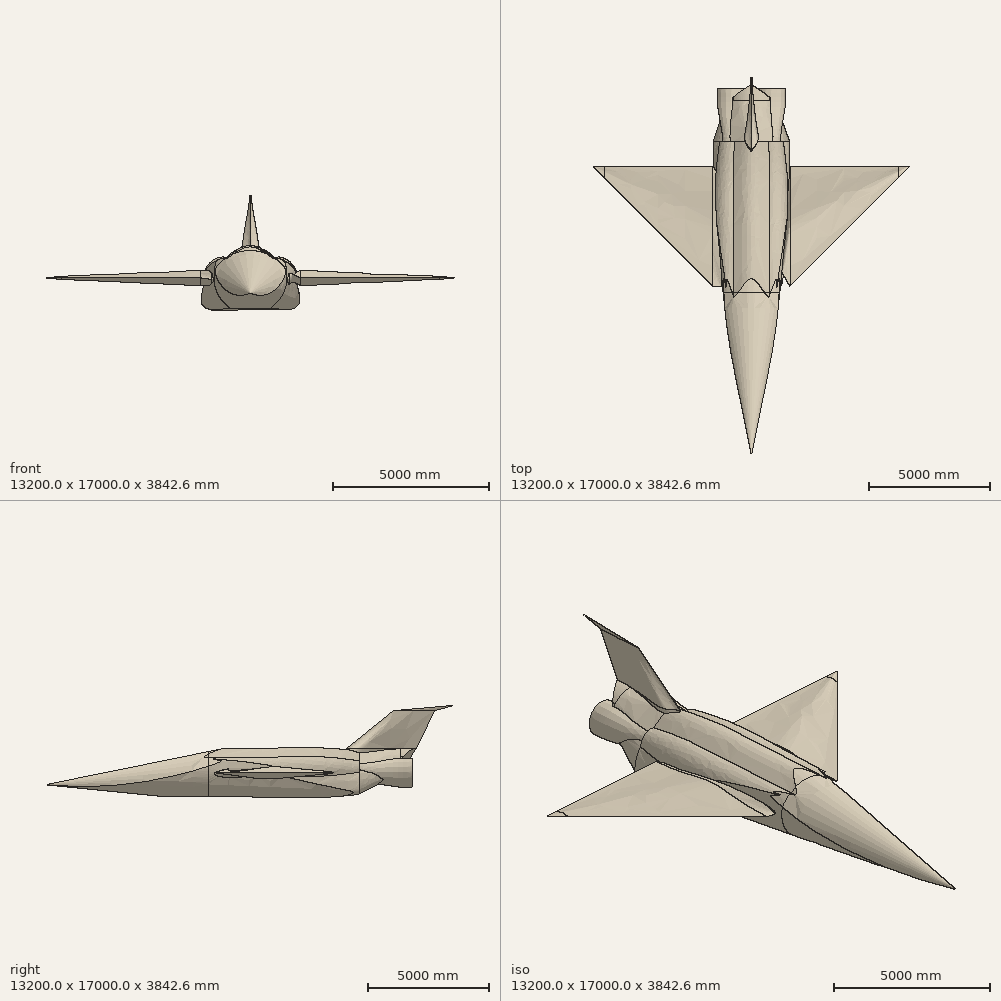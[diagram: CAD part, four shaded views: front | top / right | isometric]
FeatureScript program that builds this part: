
annotation { "Feature Type Name" : "Feature", "Feature Type Description" : "" }
export const myFeature = defineFeature(function(context is Context, id is Id, definition is map)
    precondition{}
    {
        {
            var Q0;
            Q0=qCreatedBy(makeId("Front.planeOp"),FACE);
            cPlane(context, id + "F0", {"entities" : qUnion([Q0]), "cplaneType" : CPlaneType.OFFSET, "offset" : 1750 * mm, "width" : 152.4 * mm, "height" : 152.4 * mm});
        }
        {
            var Q0;
            Q0=qCreatedBy(id+"F0.planeOp",FACE);
            var sketch = newSketch(context, id + "F1", { "sketchPlane" : qUnion([Q0])});
            skLineSegment(sketch, "E0.top", {"start": v(-1394.2, -1000) * mm, "end": v(1394.2, -1000) * mm});
            skPoint(sketch, "E0.middle", {"position": v(0, 0) * mm});
            skFitSpline(sketch, "E1", {"points": [v(-1600, -1000) * mm, v(-848, 530) * mm, v(0, 1000) * mm, v(848, 530) * mm, v(1600, -1000) * mm], "startDerivative": vector(0, 10524.75) * mm, "endDerivative": vector(0, -10524.75) * mm});
            skArc(sketch, "E2", {"start": v(-735.27, 618.52) * mm, "mid": v(-1273.27, 435.52) * mm, "end": v(-1440.68, -107.53) * mm});
            skArc(sketch, "E3.trimOffspring", {"start": v(1440.68, -107.53) * mm, "mid": v(1273.27, 435.52) * mm, "end": v(735.27, 618.52) * mm});
            skFitSpline(sketch, "E4.trimOffspring", {"points": [v(-1600, -1000) * mm, v(-848, 530) * mm, v(0, 1000) * mm, v(848, 530) * mm, v(1600, -1000) * mm], "startDerivative": vector(0, 10524.75) * mm, "endDerivative": vector(0, -10524.75) * mm});
            skFitSpline(sketch, "E5.trimOffspring", {"points": [v(-1600, -1000) * mm, v(-848, 530) * mm, v(0, 1000) * mm, v(848, 530) * mm, v(1600, -1000) * mm], "startDerivative": vector(0, 10524.75) * mm, "endDerivative": vector(0, -10524.75) * mm});
            skArc(sketch, "E6.filletArc", {"start": v(-1593.82, -787.83) * mm, "mid": v(-1539.85, -937.05) * mm, "end": v(-1394.2, -1000) * mm});
            skArc(sketch, "E7.filletArc", {"start": v(1394.2, -1000) * mm, "mid": v(1539.85, -937.05) * mm, "end": v(1593.82, -787.83) * mm});
            skSolve(sketch);
        }
        {
            var Q0;
            Q0=qCreatedBy(makeId("Front.planeOp"),FACE);
            var sketch = newSketch(context, id + "F2", { "sketchPlane" : qUnion([Q0])});
            skLineSegment(sketch, "E8.top", {"start": v(-1394.2, -1000) * mm, "end": v(1394.2, -1000) * mm});
            skPoint(sketch, "E8.middle", {"position": v(0, 0) * mm});
            skFitSpline(sketch, "E9", {"points": [v(-1600, -1000) * mm, v(-848, 530) * mm, v(0, 1000) * mm, v(848, 530) * mm, v(1600, -1000) * mm], "startDerivative": vector(0, 10524.75) * mm, "endDerivative": vector(0, -10524.75) * mm});
            skArc(sketch, "E10", {"start": v(-735.27, 618.52) * mm, "mid": v(-1273.27, 435.52) * mm, "end": v(-1440.68, -107.53) * mm});
            skArc(sketch, "E11.trimOffspring", {"start": v(1440.68, -107.53) * mm, "mid": v(1273.27, 435.52) * mm, "end": v(735.27, 618.52) * mm});
            skFitSpline(sketch, "E12.trimOffspring", {"points": [v(-1600, -1000) * mm, v(-848, 530) * mm, v(0, 1000) * mm, v(848, 530) * mm, v(1600, -1000) * mm], "startDerivative": vector(0, 10524.75) * mm, "endDerivative": vector(0, -10524.75) * mm});
            skFitSpline(sketch, "E13.trimOffspring", {"points": [v(-1600, -1000) * mm, v(-848, 530) * mm, v(0, 1000) * mm, v(848, 530) * mm, v(1600, -1000) * mm], "startDerivative": vector(0, 10524.75) * mm, "endDerivative": vector(0, -10524.75) * mm});
            skArc(sketch, "E14.filletArc", {"start": v(-1593.82, -787.83) * mm, "mid": v(-1539.85, -937.05) * mm, "end": v(-1394.2, -1000) * mm});
            skArc(sketch, "E15.filletArc", {"start": v(1394.2, -1000) * mm, "mid": v(1539.85, -937.05) * mm, "end": v(1593.82, -787.83) * mm});
            skSolve(sketch);
        }
        {
            var Q0;
            Q0=qCreatedBy(makeId("Front.planeOp"),FACE);
            cPlane(context, id + "F3", {"entities" : qUnion([Q0]), "cplaneType" : CPlaneType.OFFSET, "offset" : 3500 * mm, "oppositeDirection" : true, "width" : 150 * mm, "height" : 150 * mm});
        }
        {
            var Q0;
            Q0=qCreatedBy(id+"F3.planeOp",FACE);
            var sketch = newSketch(context, id + "F4", { "sketchPlane" : qUnion([Q0])});
            skLineSegment(sketch, "E16.top", {"start": v(-1394.2, -1000) * mm, "end": v(1394.2, -1000) * mm});
            skPoint(sketch, "E16.middle", {"position": v(0, 0) * mm});
            skFitSpline(sketch, "E17", {"points": [v(-1600, -1000) * mm, v(-848, 530) * mm, v(0, 1000) * mm, v(848, 530) * mm, v(1600, -1000) * mm], "startDerivative": vector(0, 10524.75) * mm, "endDerivative": vector(0, -10524.75) * mm});
            skArc(sketch, "E18", {"start": v(-735.27, 618.52) * mm, "mid": v(-1273.27, 435.52) * mm, "end": v(-1440.68, -107.53) * mm});
            skArc(sketch, "E19.trimOffspring", {"start": v(1440.68, -107.53) * mm, "mid": v(1273.27, 435.52) * mm, "end": v(735.27, 618.52) * mm});
            skFitSpline(sketch, "E20.trimOffspring", {"points": [v(-1600, -1000) * mm, v(-848, 530) * mm, v(0, 1000) * mm, v(848, 530) * mm, v(1600, -1000) * mm], "startDerivative": vector(0, 10524.75) * mm, "endDerivative": vector(0, -10524.75) * mm});
            skFitSpline(sketch, "E21.trimOffspring", {"points": [v(-1600, -1000) * mm, v(-848, 530) * mm, v(0, 1000) * mm, v(848, 530) * mm, v(1600, -1000) * mm], "startDerivative": vector(0, 10524.75) * mm, "endDerivative": vector(0, -10524.75) * mm});
            skArc(sketch, "E22.filletArc", {"start": v(-1593.82, -787.83) * mm, "mid": v(-1539.85, -937.05) * mm, "end": v(-1394.2, -1000) * mm});
            skArc(sketch, "E23.filletArc", {"start": v(1394.2, -1000) * mm, "mid": v(1539.85, -937.05) * mm, "end": v(1593.82, -787.83) * mm});
            skSolve(sketch);
        }
        {
            var Q0;
            Q0=qCreatedBy(makeId("Front.planeOp"),FACE);
            cPlane(context, id + "F5", {"entities" : qUnion([Q0]), "cplaneType" : CPlaneType.OFFSET, "offset" : 4500 * mm, "oppositeDirection" : true, "width" : 150 * mm, "height" : 150 * mm});
        }
        {
            var Q0;
            Q0=qCreatedBy(id+"F5.planeOp",FACE);
            var sketch = newSketch(context, id + "F6", { "sketchPlane" : qUnion([Q0])});
            skLineSegment(sketch, "E24.top", {"start": v(-1413.07, -900) * mm, "end": v(1413.07, -900) * mm});
            skPoint(sketch, "E24.middle", {"position": v(0, 0) * mm});
            skFitSpline(sketch, "E25", {"points": [v(-1600, -900) * mm, v(-784.42, 441.24) * mm, v(0, 900) * mm, v(784.42, 441.24) * mm, v(1600, -900) * mm], "startDerivative": vector(0, 9508.62) * mm, "endDerivative": vector(0, -9508.62) * mm});
            skArc(sketch, "E26", {"start": v(-719.25, 488.69) * mm, "mid": v(-1131.76, 394.84) * mm, "end": v(-1324.66, 18.33) * mm});
            skArc(sketch, "E27.trimOffspring", {"start": v(1324.66, 18.33) * mm, "mid": v(1131.76, 394.84) * mm, "end": v(719.25, 488.69) * mm});
            skFitSpline(sketch, "E28.trimOffspring", {"points": [v(-1600, -900) * mm, v(-784.42, 441.24) * mm, v(0, 900) * mm, v(784.42, 441.24) * mm, v(1600, -900) * mm], "startDerivative": vector(0, 9508.62) * mm, "endDerivative": vector(0, -9508.62) * mm});
            skFitSpline(sketch, "E29.trimOffspring", {"points": [v(-1600, -900) * mm, v(-784.42, 441.24) * mm, v(0, 900) * mm, v(784.42, 441.24) * mm, v(1600, -900) * mm], "startDerivative": vector(0, 9508.62) * mm, "endDerivative": vector(0, -9508.62) * mm});
            skArc(sketch, "E30.filletArc", {"start": v(-1592.48, -705.43) * mm, "mid": v(-1545.4, -842.02) * mm, "end": v(-1413.07, -900) * mm});
            skArc(sketch, "E31.filletArc", {"start": v(1413.07, -900) * mm, "mid": v(1545.4, -842.02) * mm, "end": v(1592.48, -705.43) * mm});
            skLineSegment(sketch, "E32", {"start": v(-719.25, 488.69) * mm, "end": v(-1324.66, 18.33) * mm, "construction": true});
            skLineSegment(sketch, "E33", {"start": v(719.25, 488.69) * mm, "end": v(1324.66, 18.33) * mm, "construction": true});
            skSolve(sketch);
        }
        {
            var Q0;
            Q0=qCreatedBy(makeId("Front.planeOp"),FACE);
            cPlane(context, id + "F7", {"entities" : qUnion([Q0]), "cplaneType" : CPlaneType.OFFSET, "offset" : 6232.05 * mm, "oppositeDirection" : true, "width" : 150 * mm, "height" : 150 * mm});
        }
        {
            var Q0;
            Q0=qCreatedBy(id+"F7.planeOp",FACE);
            var sketch = newSketch(context, id + "F8", { "sketchPlane" : qUnion([Q0])});
            skArc(sketch, "E34", {"start": v(998.61, 52.63) * mm, "mid": v(0, 1000) * mm, "end": v(-998.61, 52.63) * mm});
            skLineSegment(sketch, "E35", {"start": v(0, 0) * mm, "end": v(-948.68, 0) * mm});
            skLineSegment(sketch, "E36", {"start": v(0, 0) * mm, "end": v(948.68, 0) * mm});
            skPoint(sketch, "E37.visualSharp", {"position": v(-1000, 0) * mm});
            skArc(sketch, "E37.filletArc", {"start": v(-998.61, 52.63) * mm, "mid": v(-984.96, 15.59) * mm, "end": v(-948.68, 0) * mm});
            skPoint(sketch, "E38.visualSharp", {"position": v(1000, 0) * mm});
            skArc(sketch, "E38.filletArc", {"start": v(948.68, 0) * mm, "mid": v(984.96, 15.59) * mm, "end": v(998.61, 52.63) * mm});
            skLineSegment(sketch, "E39", {"start": v(0, 1000) * mm, "end": v(0, 675) * mm, "construction": true});
            skPoint(sketch, "E39.endSnap0", {"position": v(0, 1000) * mm});
            skLineSegment(sketch, "E40", {"start": v(0, 675) * mm, "end": v(737.82, 675) * mm, "construction": true});
            skLineSegment(sketch, "E41", {"start": v(0, 675) * mm, "end": v(-737.82, 675) * mm, "construction": true});
            skSolve(sketch);
        }
        {
            var Q0;
            Q0=qSketchRegion(id+"F1",true);
            var Q1;
            Q1=qSketchRegion(id+"F2",true);
            var Q2;
            Q2=qSketchRegion(id+"F4",true);
            var Q3;
            Q3=qSketchRegion(id+"F6",true);
            loft(context, id + "F9", {"sheetProfilesArray" : [{ "sheetProfileEntities" : qUnion([Q0]) }, { "sheetProfileEntities" : qUnion([Q1]) }, { "sheetProfileEntities" : qUnion([Q2]) }, { "sheetProfileEntities" : qUnion([Q3]) }]});
        }
        {
            var Q0;
            Q0=sQuery(id+"F6.wireOp",EDGE,"E32");
            var Q1;
            Q1=sQuery(id+"F8.wireOp",VERTEX,"E41.end");
            cPlane(context, id + "F10", {"entities" : qUnion([Q0, Q1]), "cplaneType" : CPlaneType.LINE_ANGLE, "offset" : 25 * mm, "angle" : 0 * degree, "width" : 150 * mm, "height" : 150 * mm});
        }
        {
            var Q0;
            Q0=qCreatedBy(id+"F10.planeOp",FACE);
            var sketch = newSketch(context, id + "F11", { "sketchPlane" : qUnion([Q0])});
            skLineSegment(sketch, "E42", {"start": v(-589.34, -4526.34) * mm, "end": v(-612.8, -6268.32) * mm});
            skLineSegment(sketch, "E43", {"start": v(-1354.08, -4472.19) * mm, "end": v(-612.8, -6268.32) * mm});
            skSolve(sketch);
        }
        {
            var Q0;
            Q0=sQuery(id+"F6.wireOp",EDGE,"E33");
            var Q1;
            Q1=sQuery(id+"F8.wireOp",VERTEX,"E40.end");
            cPlane(context, id + "F12", {"entities" : qUnion([Q0, Q1]), "cplaneType" : CPlaneType.LINE_ANGLE, "offset" : 25 * mm, "angle" : 0 * degree, "width" : 150 * mm, "height" : 150 * mm});
        }
        {
            var Q0;
            Q0=qCreatedBy(id+"F12.planeOp",FACE);
            var sketch = newSketch(context, id + "F13", { "sketchPlane" : qUnion([Q0])});
            skLineSegment(sketch, "E44", {"start": v(589.34, 4526.34) * mm, "end": v(612.8, 6268.32) * mm});
            skLineSegment(sketch, "E45", {"start": v(1354.08, 4472.19) * mm, "end": v(612.8, 6268.32) * mm});
            skSolve(sketch);
        }
        {
            var Q1;
            Q1=makeQuery(id+"F6.imprint","IMPRINT",FACE,{"disambiguationData":[TD([[makeQuery(id+"F6.imprint","IMPRINT",EDGE,{"derivedFrom":sQuery(id+"F6.wireOp",EDGE,"E24.top")}),1.0]])]});
            var Q2;
            Q2=makeQuery(id+"F8.imprint","IMPRINT",FACE,{"disambiguationData":[TD([[makeQuery(id+"F8.imprint","IMPRINT",EDGE,{"derivedFrom":sQuery(id+"F8.wireOp",EDGE,"E34")}),1.0]])]});
            var Q3;
            Q3=sQuery(id+"F11.wireOp",EDGE,"E42");
            var Q4;
            Q4=sQuery(id+"F13.wireOp",EDGE,"E44");
            loft(context, id + "F14", {"operationType" : NewBodyOperationType.ADD, "addGuides" : true, "sheetProfilesArray" : [{ "sheetProfileEntities" : qUnion([Q1]) }, { "sheetProfileEntities" : qUnion([Q2]) }], "guidesArray" : [{ "guideEntities" : qUnion([Q3]), "guideDerivativeType" : LoftGuideDerivativeType.DEFAULT, "guideDerivativeMagnitude" : 1 }, { "guideEntities" : qUnion([Q4]), "guideDerivativeType" : LoftGuideDerivativeType.DEFAULT, "guideDerivativeMagnitude" : 1 }]});
        }
        {
            var Q0;
            Q0=makeQuery(id+"F14.opLoft","CAP_FACE",FACE,{"disambiguationData":[OSD([makeQuery(id+"F8.imprint","IMPRINT",FACE,{"disambiguationData":[TD([[makeQuery(id+"F8.imprint","IMPRINT",EDGE,{"derivedFrom":sQuery(id+"F8.wireOp",EDGE,"E34")}),1.0]])]})])],"isStart":true});
            extrude(context, id + "F15", {"entities" : qUnion([Q0]), "operationType" : NewBodyOperationType.ADD, "depth" : 649.4 * mm});
        }
        {
            var Q0;
            Q0=qCreatedBy(makeId("Right.planeOp"),FACE);
            var sketch = newSketch(context, id + "F16", { "sketchPlane" : qUnion([Q0])});
            skLineSegment(sketch, "E46", {"start": v(0, 0) * mm, "end": v(4500, 0) * mm});
            skLineSegment(sketch, "E47", {"start": v(4500, 0) * mm, "end": v(6232.05, 0) * mm});
            skLineSegment(sketch, "E48", {"start": v(4500, 0) * mm, "end": v(4500, 1000) * mm});
            skLineSegment(sketch, "E49", {"start": v(4500, 1000) * mm, "end": v(6881.46, 1000) * mm});
            skLineSegment(sketch, "E50", {"start": v(6881.46, 1000) * mm, "end": v(6881.46, -1000) * mm});
            skLineSegment(sketch, "E51", {"start": v(6881.46, 1000) * mm, "end": v(6232.05, 0) * mm});
            skLineSegment(sketch, "E52", {"start": v(6232.05, 0) * mm, "end": v(5582.64, -1000) * mm});
            skLineSegment(sketch, "E53", {"start": v(5582.64, -1000) * mm, "end": v(6881.46, -1000) * mm});
            skSolve(sketch);
        }
        {
            var Q0;
            Q0=makeQuery(id+"F16.imprint","IMPRINT",FACE,{"disambiguationData":[TD([[makeQuery(id+"F16.imprint","IMPRINT",EDGE,{"derivedFrom":sQuery(id+"F16.wireOp",EDGE,"E50")}),-1.0]])]});
            var Q1;
            Q1=sQuery(id+"F16.wireOp",EDGE,"E49");
            revolve(context, id + "F17", {"operationType" : NewBodyOperationType.REMOVE, "entities" : qUnion([Q0]), "axis" : qUnion([Q1]), "revolveType" : RevolveType.SYMMETRIC, "oppositeDirection" : true, "angle" : 182 * degree});
        }
        {
            var Q0;
            Q0=makeQuery(id+"F9.opLoft","CAP_FACE",FACE,{"disambiguationData":[OSD([makeQuery(id+"F1.imprint","IMPRINT",FACE,{"disambiguationData":[TD([[makeQuery(id+"F1.imprint","IMPRINT",EDGE,{"derivedFrom":sQuery(id+"F1.wireOp",EDGE,"E0.top")}),1.0]])]})])],"isStart":true});
            extrude(context, id + "F18", {"entities" : qUnion([Q0]), "depth" : 6750 * mm});
        }
        {
            var Q0;
            Q0=qCreatedBy(makeId("Right.planeOp"),FACE);
            var sketch = newSketch(context, id + "F19", { "sketchPlane" : qUnion([Q0])});
            skLineSegment(sketch, "E54", {"start": v(0, 0) * mm, "end": v(-3500, 0) * mm});
            skLineSegment(sketch, "E55", {"start": v(-3500, 0) * mm, "end": v(-3500, -1000) * mm});
            skLineSegment(sketch, "E56", {"start": v(-3500, -1000) * mm, "end": v(-8500, -1000) * mm});
            skLineSegment(sketch, "E57", {"start": v(-8500, -1000) * mm, "end": v(-8500, -499.31) * mm});
            skLineSegment(sketch, "E58", {"start": v(-1151.4, 0) * mm, "end": v(-1151.4, 1000) * mm});
            skLineSegment(sketch, "E59", {"start": v(-1151.4, 1000) * mm, "end": v(-8500, -499.31) * mm});
            skLineSegment(sketch, "E60", {"start": v(-8500, -499.31) * mm, "end": v(-3500, -1000) * mm});
            skLineSegment(sketch, "E61", {"start": v(-1151.4, 1000) * mm, "end": v(-8500, 1000) * mm});
            skLineSegment(sketch, "E62", {"start": v(-8500, 1000) * mm, "end": v(-8500, -499.31) * mm});
            skLineSegment(sketch, "E63", {"start": v(-8500, -1000) * mm, "end": v(-8500, -1980) * mm});
            skLineSegment(sketch, "E64", {"start": v(-3500, -1000) * mm, "end": v(6286.5, -1980) * mm});
            skLineSegment(sketch, "E65", {"start": v(6286.5, -1980) * mm, "end": v(-8500, -1980) * mm});
            skLineSegment(sketch, "E66", {"start": v(-8500, -499.31) * mm, "end": v(-3500, -499.31) * mm});
            skSolve(sketch);
        }
        {
            var Q0;
            Q0=makeQuery(id+"F19.imprint","IMPRINT",FACE,{"disambiguationData":[TD([[makeQuery(id+"F19.imprint","IMPRINT",EDGE,{"derivedFrom":sQuery(id+"F19.wireOp",EDGE,"E59")}),-1.0]])]});
            var Q1;
            Q1=sQuery(id+"F19.wireOp",EDGE,"E66");
            revolve(context, id + "F20", {"operationType" : NewBodyOperationType.REMOVE, "entities" : qUnion([Q0]), "axis" : qUnion([Q1]), "revolveType" : RevolveType.SYMMETRIC, "oppositeDirection" : true, "angle" : 250 * degree});
        }
        {
            var Q0;
            Q0=makeQuery(id+"F19.imprint","IMPRINT",FACE,{"disambiguationData":[TD([[makeQuery(id+"F19.imprint","IMPRINT",EDGE,{"derivedFrom":sQuery(id+"F19.wireOp",EDGE,"E56")}),-1.0]])]});
            var Q1;
            Q1=makeQuery(id+"F19.imprint","IMPRINT",FACE,{"disambiguationData":[TD([[makeQuery(id+"F19.imprint","IMPRINT",EDGE,{"derivedFrom":sQuery(id+"F19.wireOp",EDGE,"E56")}),1.0]])]});
            var Q2;
            Q2=sQuery(id+"F19.wireOp",EDGE,"E54");
            revolve(context, id + "F21", {"operationType" : NewBodyOperationType.REMOVE, "entities" : qUnion([Q0, Q1]), "axis" : qUnion([Q2]), "revolveType" : RevolveType.SYMMETRIC, "oppositeDirection" : true, "angle" : 240 * degree});
        }
        {
            var Q0;
            Q0=qCreatedBy(makeId("Front.planeOp"),FACE);
            cPlane(context, id + "F22", {"entities" : qUnion([Q0]), "cplaneType" : CPlaneType.OFFSET, "offset" : 3500 * mm, "oppositeDirection" : true, "width" : 150 * mm, "height" : 150 * mm});
        }
        {
            var Q0;
            Q0=qCreatedBy(id+"F22.planeOp",FACE);
            var sketch = newSketch(context, id + "F23", { "sketchPlane" : qUnion([Q0])});
            skCircle(sketch, "E67", {"center": v(-825, 0) * mm, "radius": 600 * mm});
            skCircle(sketch, "E68", {"center": v(825, 0) * mm, "radius": 600 * mm});
            skSolve(sketch);
        }
        {
            var Q0;
            Q0=qCreatedBy(makeId("Front.planeOp"),FACE);
            cPlane(context, id + "F24", {"entities" : qUnion([Q0]), "cplaneType" : CPlaneType.OFFSET, "offset" : 4500 * mm, "oppositeDirection" : true, "width" : 150 * mm, "height" : 150 * mm});
        }
        {
            var Q0;
            Q0=qCreatedBy(id+"F24.planeOp",FACE);
            var sketch = newSketch(context, id + "F25", { "sketchPlane" : qUnion([Q0])});
            skCircle(sketch, "E69", {"center": v(-825, 0) * mm, "radius": 400 * mm});
            skCircle(sketch, "E70", {"center": v(825, 0) * mm, "radius": 400 * mm});
            skSolve(sketch);
        }
        {
            var Q0;
            Q0=qCreatedBy(makeId("Front.planeOp"),FACE);
            cPlane(context, id + "F26", {"entities" : qUnion([Q0]), "cplaneType" : CPlaneType.OFFSET, "offset" : 6232.05 * mm, "oppositeDirection" : true, "width" : 150 * mm, "height" : 150 * mm});
        }
        {
            var Q0;
            Q0=qCreatedBy(id+"F26.planeOp",FACE);
            var sketch = newSketch(context, id + "F27", { "sketchPlane" : qUnion([Q0])});
            skCircle(sketch, "E71", {"center": v(-825, 0) * mm, "radius": 600 * mm});
            skCircle(sketch, "E72", {"center": v(825, 0) * mm, "radius": 600 * mm});
            skSolve(sketch);
        }
        {
            var Q0;
            Q0=qCreatedBy(makeId("Front.planeOp"),FACE);
            cPlane(context, id + "F28", {"entities" : qUnion([Q0]), "cplaneType" : CPlaneType.OFFSET, "offset" : 6732.05 * mm, "oppositeDirection" : true, "width" : 150 * mm, "height" : 150 * mm});
        }
        {
            var Q0;
            Q0=qCreatedBy(id+"F28.planeOp",FACE);
            var sketch = newSketch(context, id + "F29", { "sketchPlane" : qUnion([Q0])});
            skCircle(sketch, "E73", {"center": v(-825, 0) * mm, "radius": 600 * mm});
            skCircle(sketch, "E74", {"center": v(825, 0) * mm, "radius": 600 * mm});
            skSolve(sketch);
        }
        {
            var Q0;
            Q0=makeQuery(id+"F23.imprint","IMPRINT",FACE,{"disambiguationData":[TD([[makeQuery(id+"F23.imprint","IMPRINT",EDGE,{"derivedFrom":sQuery(id+"F23.wireOp",EDGE,"E67")}),1.0]])]});
            var Q1;
            Q1=makeQuery(id+"F25.imprint","IMPRINT",FACE,{"disambiguationData":[TD([[makeQuery(id+"F25.imprint","IMPRINT",EDGE,{"derivedFrom":sQuery(id+"F25.wireOp",EDGE,"E69")}),1.0]])]});
            var Q2;
            Q2=makeQuery(id+"F27.imprint","IMPRINT",FACE,{"disambiguationData":[TD([[makeQuery(id+"F27.imprint","IMPRINT",EDGE,{"derivedFrom":sQuery(id+"F27.wireOp",EDGE,"E71")}),1.0]])]});
            var Q3;
            Q3=makeQuery(id+"F29.imprint","IMPRINT",FACE,{"disambiguationData":[TD([[makeQuery(id+"F29.imprint","IMPRINT",EDGE,{"derivedFrom":sQuery(id+"F29.wireOp",EDGE,"E73")}),1.0]])]});
            loft(context, id + "F30", {"sheetProfilesArray" : [{ "sheetProfileEntities" : qUnion([Q0]) }, { "sheetProfileEntities" : qUnion([Q1]) }, { "sheetProfileEntities" : qUnion([Q2]) }, { "sheetProfileEntities" : qUnion([Q3]) }]});
        }
        {
            var Q0;
            Q0=makeQuery(id+"F23.imprint","IMPRINT",FACE,{"disambiguationData":[TD([[makeQuery(id+"F23.imprint","IMPRINT",EDGE,{"derivedFrom":sQuery(id+"F23.wireOp",EDGE,"E68")}),1.0]])]});
            var Q1;
            Q1=makeQuery(id+"F25.imprint","IMPRINT",FACE,{"disambiguationData":[TD([[makeQuery(id+"F25.imprint","IMPRINT",EDGE,{"derivedFrom":sQuery(id+"F25.wireOp",EDGE,"E70")}),1.0]])]});
            var Q2;
            Q2=makeQuery(id+"F27.imprint","IMPRINT",FACE,{"disambiguationData":[TD([[makeQuery(id+"F27.imprint","IMPRINT",EDGE,{"derivedFrom":sQuery(id+"F27.wireOp",EDGE,"E72")}),1.0]])]});
            var Q3;
            Q3=makeQuery(id+"F29.imprint","IMPRINT",FACE,{"disambiguationData":[TD([[makeQuery(id+"F29.imprint","IMPRINT",EDGE,{"derivedFrom":sQuery(id+"F29.wireOp",EDGE,"E74")}),1.0]])]});
            loft(context, id + "F31", {"sheetProfilesArray" : [{ "sheetProfileEntities" : qUnion([Q0]) }, { "sheetProfileEntities" : qUnion([Q1]) }, { "sheetProfileEntities" : qUnion([Q2]) }, { "sheetProfileEntities" : qUnion([Q3]) }]});
        }
        {
            var Q0;
            Q0=qCreatedBy(makeId("Top.planeOp"),FACE);
            var sketch = newSketch(context, id + "F32", { "sketchPlane" : qUnion([Q0])});
            skLineSegment(sketch, "E75", {"start": v(0, 0) * mm, "end": v(0, 1000) * mm});
            skLineSegment(sketch, "E76", {"start": v(0, 1000) * mm, "end": v(-1600, 1000) * mm});
            skLineSegment(sketch, "E77", {"start": v(-1600, 1000) * mm, "end": v(-1600, -1500) * mm});
            skLineSegment(sketch, "E78", {"start": v(-1600, 1000) * mm, "end": v(-1600, 3500) * mm});
            skLineSegment(sketch, "E79", {"start": v(-1600, 3500) * mm, "end": v(-6100, 3500) * mm});
            skLineSegment(sketch, "E80", {"start": v(-6100, 3500) * mm, "end": v(-6600, 3500) * mm});
            skLineSegment(sketch, "E81", {"start": v(-6100, 3500) * mm, "end": v(-6100, 3000) * mm});
            skLineSegment(sketch, "E82", {"start": v(-1600, -1500) * mm, "end": v(-6100, 3000) * mm});
            skLineSegment(sketch, "E83", {"start": v(0, 1000) * mm, "end": v(1600, 1000) * mm});
            skLineSegment(sketch, "E84", {"start": v(1600, 1000) * mm, "end": v(1600, -1500) * mm});
            skLineSegment(sketch, "E85", {"start": v(1600, 1000) * mm, "end": v(1600, 3500) * mm});
            skLineSegment(sketch, "E86", {"start": v(1600, 3500) * mm, "end": v(6100, 3500) * mm});
            skLineSegment(sketch, "E87", {"start": v(6100, 3500) * mm, "end": v(6600, 3500) * mm});
            skLineSegment(sketch, "E88", {"start": v(6100, 3500) * mm, "end": v(6100, 3000) * mm});
            skLineSegment(sketch, "E89", {"start": v(1600, -1500) * mm, "end": v(6100, 3000) * mm});
            skSolve(sketch);
        }
        {
            var Q0;
            Q0=qCreatedBy(makeId("Right.planeOp"),FACE);
            var sketch = newSketch(context, id + "F33", { "sketchPlane" : qUnion([Q0])});
            skFitSpline(sketch, "E90", {"points": [v(-1500, -50) * mm, v(0, 250) * mm, v(3000, -50) * mm, v(0, -250) * mm, v(-1500, -50) * mm]});
            skSolve(sketch);
        }
        {
            var Q0;
            Q0=qCreatedBy(makeId("Right.planeOp"),FACE);
            cPlane(context, id + "F34", {"entities" : qUnion([Q0]), "cplaneType" : CPlaneType.OFFSET, "offset" : 1600 * mm, "oppositeDirection" : true, "width" : 150 * mm, "height" : 150 * mm});
        }
        {
            var Q0;
            Q0=qCreatedBy(id+"F34.planeOp",FACE);
            var sketch = newSketch(context, id + "F35", { "sketchPlane" : qUnion([Q0])});
            skFitSpline(sketch, "E91", {"points": [v(-1500, 0) * mm, v(1000, 250) * mm, v(3500, 0) * mm], "startDerivative": vector(7500, 0) * mm, "endDerivative": vector(7500, 0) * mm});
            skFitSpline(sketch, "E92", {"points": [v(-1500, 0) * mm, v(1000, -250) * mm, v(3500, 0) * mm], "startDerivative": vector(5000, -750) * mm, "endDerivative": vector(7500, 0) * mm});
            skSolve(sketch);
        }
        {
            var Q0;
            Q0=qCreatedBy(makeId("Right.planeOp"),FACE);
            cPlane(context, id + "F36", {"entities" : qUnion([Q0]), "cplaneType" : CPlaneType.OFFSET, "offset" : 1600 * mm, "width" : 150 * mm, "height" : 150 * mm});
        }
        {
            var Q0;
            Q0=qCreatedBy(id+"F36.planeOp",FACE);
            var sketch = newSketch(context, id + "F37", { "sketchPlane" : qUnion([Q0])});
            skFitSpline(sketch, "E93", {"points": [v(-1500, 0) * mm, v(1000, 250) * mm, v(3500, 0) * mm], "startDerivative": vector(7500, 0) * mm, "endDerivative": vector(7500, 0) * mm});
            skFitSpline(sketch, "E94", {"points": [v(-1500, 0) * mm, v(1000, -250) * mm, v(3500, 0) * mm], "startDerivative": vector(5000, -750) * mm, "endDerivative": vector(7500, 0) * mm});
            skSolve(sketch);
        }
        {
            var Q0;
            Q0=qCreatedBy(makeId("Right.planeOp"),FACE);
            cPlane(context, id + "F38", {"entities" : qUnion([Q0]), "cplaneType" : CPlaneType.OFFSET, "offset" : 6100 * mm, "oppositeDirection" : true, "width" : 150 * mm, "height" : 150 * mm});
        }
        {
            var Q0;
            Q0=qCreatedBy(id+"F38.planeOp",FACE);
            var sketch = newSketch(context, id + "F39", { "sketchPlane" : qUnion([Q0])});
            skFitSpline(sketch, "E95", {"points": [v(3000, 0) * mm, v(3250, 50) * mm, v(3500, 0) * mm], "startDerivative": vector(750, 0) * mm, "endDerivative": vector(750, 0) * mm});
            skFitSpline(sketch, "E96", {"points": [v(3000, 0) * mm, v(3250, -50) * mm, v(3500, 0) * mm], "startDerivative": vector(500, -150) * mm, "endDerivative": vector(750, 0) * mm});
            skSolve(sketch);
        }
        {
            var Q0;
            Q0=qCreatedBy(makeId("Right.planeOp"),FACE);
            cPlane(context, id + "F40", {"entities" : qUnion([Q0]), "cplaneType" : CPlaneType.OFFSET, "offset" : 6100 * mm, "width" : 150 * mm, "height" : 150 * mm});
        }
        {
            var Q0;
            Q0=qCreatedBy(id+"F40.planeOp",FACE);
            var sketch = newSketch(context, id + "F41", { "sketchPlane" : qUnion([Q0])});
            skFitSpline(sketch, "E97", {"points": [v(3000, 0) * mm, v(3250, 50) * mm, v(3500, 0) * mm], "startDerivative": vector(850.99, 0) * mm, "endDerivative": vector(750, 0) * mm});
            skFitSpline(sketch, "E98", {"points": [v(3000, 0) * mm, v(3250, -50) * mm, v(3500, 0) * mm], "startDerivative": vector(500, -150) * mm, "endDerivative": vector(750, 0) * mm});
            skSolve(sketch);
        }
        {
            var Q0;
            Q0=qSketchRegion(id+"F33",true);
            extrude(context, id + "F42", {"entities" : qUnion([Q0]), "endBound" : BoundingType.SYMMETRIC, "depth" : 2500 * mm});
        }
        {
            var Q1;
            Q1=makeQuery(id+"F42.opExtrude","CAP_FACE",FACE,{"disambiguationData":[OSD([sQuery(id+"F33.wireOp",EDGE,"E90")])],"isStart":true});
            var Q2;
            {var subQ0=sQuery(id+"F35.wireOp",EDGE,"E91");Q2=makeQuery(id+"F35.imprint","IMPRINT",FACE,{"disambiguationData":[TD([[makeQuery(id+"F35.imprint","IMPRINT",EDGE,{"derivedFrom":subQ0}),-1.0]])]});}
            loft(context, id + "F43", {"operationType" : NewBodyOperationType.ADD, "sheetProfilesArray" : [{ "sheetProfileEntities" : qUnion([Q1]) }, { "sheetProfileEntities" : qUnion([Q2]) }]});
        }
        {
            var Q1;
            Q1=makeQuery(id+"F42.opExtrude","CAP_FACE",FACE,{"disambiguationData":[OSD([sQuery(id+"F33.wireOp",EDGE,"E90")])],"isStart":false});
            var Q2;
            {var subQ0=sQuery(id+"F37.wireOp",EDGE,"E93");Q2=makeQuery(id+"F37.imprint","IMPRINT",FACE,{"disambiguationData":[TD([[makeQuery(id+"F37.imprint","IMPRINT",EDGE,{"derivedFrom":subQ0}),-1.0]])]});}
            loft(context, id + "F44", {"operationType" : NewBodyOperationType.ADD, "sheetProfilesArray" : [{ "sheetProfileEntities" : qUnion([Q1]) }, { "sheetProfileEntities" : qUnion([Q2]) }]});
        }
        {
            var Q1;
            {var subQ0=sQuery(id+"F35.wireOp",EDGE,"E91");Q1=makeQuery(id+"F43.opLoft","CAP_FACE",FACE,{"disambiguationData":[OSD([makeQuery(id+"F35.imprint","IMPRINT",FACE,{"disambiguationData":[TD([[makeQuery(id+"F35.imprint","IMPRINT",EDGE,{"derivedFrom":subQ0}),-1.0]])]})])],"isStart":true});}
            var Q2;
            {var subQ0=sQuery(id+"F39.wireOp",EDGE,"E95");Q2=makeQuery(id+"F39.imprint","IMPRINT",FACE,{"disambiguationData":[TD([[makeQuery(id+"F39.imprint","IMPRINT",EDGE,{"derivedFrom":subQ0}),-1.0]])]});}
            loft(context, id + "F45", {"operationType" : NewBodyOperationType.ADD, "sheetProfilesArray" : [{ "sheetProfileEntities" : qUnion([Q1]) }, { "sheetProfileEntities" : qUnion([Q2]) }]});
        }
        {
            var Q1;
            {var subQ0=sQuery(id+"F37.wireOp",EDGE,"E93");Q1=makeQuery(id+"F44.opLoft","CAP_FACE",FACE,{"disambiguationData":[OSD([makeQuery(id+"F37.imprint","IMPRINT",FACE,{"disambiguationData":[TD([[makeQuery(id+"F37.imprint","IMPRINT",EDGE,{"derivedFrom":subQ0}),-1.0]])]})])],"isStart":true});}
            var Q2;
            {var subQ0=sQuery(id+"F41.wireOp",EDGE,"E97");Q2=makeQuery(id+"F41.imprint","IMPRINT",FACE,{"disambiguationData":[TD([[makeQuery(id+"F41.imprint","IMPRINT",EDGE,{"derivedFrom":subQ0}),-1.0]])]});}
            loft(context, id + "F46", {"operationType" : NewBodyOperationType.ADD, "sheetProfilesArray" : [{ "sheetProfileEntities" : qUnion([Q1]) }, { "sheetProfileEntities" : qUnion([Q2]) }]});
        }
        {
            var Q1;
            {var subQ0=sQuery(id+"F39.wireOp",EDGE,"E95");Q1=makeQuery(id+"F45.opLoft","CAP_FACE",FACE,{"disambiguationData":[OSD([makeQuery(id+"F39.imprint","IMPRINT",FACE,{"disambiguationData":[TD([[makeQuery(id+"F39.imprint","IMPRINT",EDGE,{"derivedFrom":subQ0}),-1.0]])]})])],"isStart":true});}
            var Q2;
            Q2=sQuery(id+"F32.wireOp",VERTEX,"E80.end");
            loft(context, id + "F47", {"operationType" : NewBodyOperationType.ADD, "sheetProfilesArray" : [{ "sheetProfileEntities" : qUnion([Q1]) }, { "sheetProfileEntities" : qUnion([Q2]) }]});
        }
        {
            var Q1;
            {var subQ0=sQuery(id+"F41.wireOp",EDGE,"E97");Q1=makeQuery(id+"F46.opLoft","CAP_FACE",FACE,{"disambiguationData":[OSD([makeQuery(id+"F41.imprint","IMPRINT",FACE,{"disambiguationData":[TD([[makeQuery(id+"F41.imprint","IMPRINT",EDGE,{"derivedFrom":subQ0}),-1.0]])]})])],"isStart":true});}
            var Q2;
            Q2=sQuery(id+"F32.wireOp",VERTEX,"E87.end");
            loft(context, id + "F48", {"operationType" : NewBodyOperationType.ADD, "sheetProfilesArray" : [{ "sheetProfileEntities" : qUnion([Q1]) }, { "sheetProfileEntities" : qUnion([Q2]) }]});
        }
        {
            var Q0;
            Q0=qCreatedBy(makeId("Right.planeOp"),FACE);
            var sketch = newSketch(context, id + "F49", { "sketchPlane" : qUnion([Q0])});
            skLineSegment(sketch, "E99", {"start": v(0, 0) * mm, "end": v(4500, 0) * mm});
            skLineSegment(sketch, "E100", {"start": v(4500, 0) * mm, "end": v(4500, 1000) * mm});
            skLineSegment(sketch, "E101", {"start": v(4500, 1000) * mm, "end": v(6881.46, 1000) * mm});
            skLineSegment(sketch, "E102", {"start": v(6881.46, 1000) * mm, "end": v(8500, 1000) * mm});
            skLineSegment(sketch, "E103", {"start": v(8500, 1000) * mm, "end": v(8500, 2800) * mm});
            skLineSegment(sketch, "E104", {"start": v(4500, 1000) * mm, "end": v(4000, 1000) * mm});
            skLineSegment(sketch, "E105", {"start": v(4500, 1000) * mm, "end": v(4500, 750) * mm});
            skLineSegment(sketch, "E106", {"start": v(4500, 750) * mm, "end": v(4000, 750) * mm});
            skLineSegment(sketch, "E107", {"start": v(4500, 750) * mm, "end": v(6250, 750) * mm});
            skLineSegment(sketch, "E108", {"start": v(4000, 1000) * mm, "end": v(5943.2, 2572.89) * mm});
            skLineSegment(sketch, "E109", {"start": v(6881.46, 1000) * mm, "end": v(7648.6, 2572.89) * mm});
            skLineSegment(sketch, "E110", {"start": v(5943.2, 2572.89) * mm, "end": v(7648.6, 2572.89) * mm});
            skSolve(sketch);
        }
        {
            var Q0;
            Q0=qCreatedBy(makeId("Top.planeOp"),FACE);
            cPlane(context, id + "F50", {"entities" : qUnion([Q0]), "cplaneType" : CPlaneType.OFFSET, "offset" : 750 * mm, "width" : 150 * mm, "height" : 150 * mm});
        }
        {
            var Q0;
            Q0=qCreatedBy(id+"F50.planeOp",FACE);
            var sketch = newSketch(context, id + "F51", { "sketchPlane" : qUnion([Q0])});
            skFitSpline(sketch, "E111", {"points": [v(0, 4000) * mm, v(-250, 4500) * mm, v(0, 6250) * mm], "startDerivative": vector(-889.86, 1147.1) * mm, "endDerivative": vector(737.87, 3164.53) * mm});
            skFitSpline(sketch, "E112", {"points": [v(0, 4000) * mm, v(250, 4500) * mm, v(0, 6250) * mm], "startDerivative": vector(889.86, 1147.1) * mm, "endDerivative": vector(-737.87, 3164.53) * mm});
            skSolve(sketch);
        }
        {
            var Q0;
            Q0=qCreatedBy(makeId("Top.planeOp"),FACE);
            cPlane(context, id + "F52", {"entities" : qUnion([Q0]), "cplaneType" : CPlaneType.OFFSET, "offset" : 1000 * mm, "width" : 150 * mm, "height" : 150 * mm});
        }
        {
            var Q0;
            Q0=qCreatedBy(id+"F52.planeOp",FACE);
            var sketch = newSketch(context, id + "F53", { "sketchPlane" : qUnion([Q0])});
            skFitSpline(sketch, "E113", {"points": [v(0, 4000) * mm, v(-250, 4500) * mm, v(0, 6881.46) * mm], "startDerivative": vector(0, 2302.24) * mm, "endDerivative": vector(0, 5298.17) * mm});
            skFitSpline(sketch, "E114", {"points": [v(0, 4000) * mm, v(250, 4500) * mm, v(0, 6881.46) * mm], "startDerivative": vector(0, 2302.24) * mm, "endDerivative": vector(0, 5298.17) * mm});
            skSolve(sketch);
        }
        {
            var Q0;
            Q0=qCreatedBy(makeId("Top.planeOp"),FACE);
            cPlane(context, id + "F54", {"entities" : qUnion([Q0]), "cplaneType" : CPlaneType.OFFSET, "offset" : 2572.89 * mm, "width" : 150 * mm, "height" : 150 * mm});
        }
        {
            var Q0;
            Q0=qCreatedBy(id+"F54.planeOp",FACE);
            var sketch = newSketch(context, id + "F55", { "sketchPlane" : qUnion([Q0])});
            skFitSpline(sketch, "E115", {"points": [v(0, 5943.2) * mm, v(-25, 6795.9) * mm, v(0, 7648.6) * mm], "startDerivative": vector(-75, 1705.4) * mm, "endDerivative": vector(75, 1705.4) * mm});
            skFitSpline(sketch, "E116", {"points": [v(0, 5943.2) * mm, v(25, 6795.9) * mm, v(0, 7648.6) * mm], "startDerivative": vector(75, 1705.4) * mm, "endDerivative": vector(-75, 1705.4) * mm});
            skSolve(sketch);
        }
        {
            var Q1;
            Q1 = qSketchRegion(id + "F51", true);
            var Q2;
            Q2 = qSketchRegion(id + "F53", true);
            loft(context, id + "F56", {"sheetProfilesArray" : [{ "sheetProfileEntities" : qUnion([Q1]) }, { "sheetProfileEntities" : qUnion([Q2]) }]});
        }
        {
            var Q1;
            {var subQ0=sQuery(id+"F53.wireOp",EDGE,"E113");Q1=makeQuery(id+"F56.opLoft","CAP_FACE",FACE,{"disambiguationData":[OSD([makeQuery(id+"F53.imprint","IMPRINT",FACE,{"disambiguationData":[TD([[makeQuery(id+"F53.imprint","IMPRINT",EDGE,{"derivedFrom":subQ0}),-1.0]])]})])],"isStart":true});}
            var Q2;
            Q2=makeQuery(id+"F55.imprint","IMPRINT",FACE,{"disambiguationData":[TD([[makeQuery(id+"F55.imprint","IMPRINT",EDGE,{"derivedFrom":sQuery(id+"F55.wireOp",EDGE,"E115")}),-1.0]])]});
            loft(context, id + "F57", {"operationType" : NewBodyOperationType.ADD, "sheetProfilesArray" : [{ "sheetProfileEntities" : qUnion([Q1]) }, { "sheetProfileEntities" : qUnion([Q2]) }]});
        }
        {
            var Q1;
            Q1=makeQuery(id+"F57.opLoft","CAP_FACE",FACE,{"disambiguationData":[OSD([makeQuery(id+"F55.imprint","IMPRINT",FACE,{"disambiguationData":[TD([[makeQuery(id+"F55.imprint","IMPRINT",EDGE,{"derivedFrom":sQuery(id+"F55.wireOp",EDGE,"E115")}),-1.0]])]})])],"isStart":true});
            var Q2;
            Q2=sQuery(id+"F49.wireOp",VERTEX,"E103.end");
            loft(context, id + "F58", {"operationType" : NewBodyOperationType.ADD, "sheetProfilesArray" : [{ "sheetProfileEntities" : qUnion([Q1]) }, { "sheetProfileEntities" : qUnion([Q2]) }]});
        }
    });
